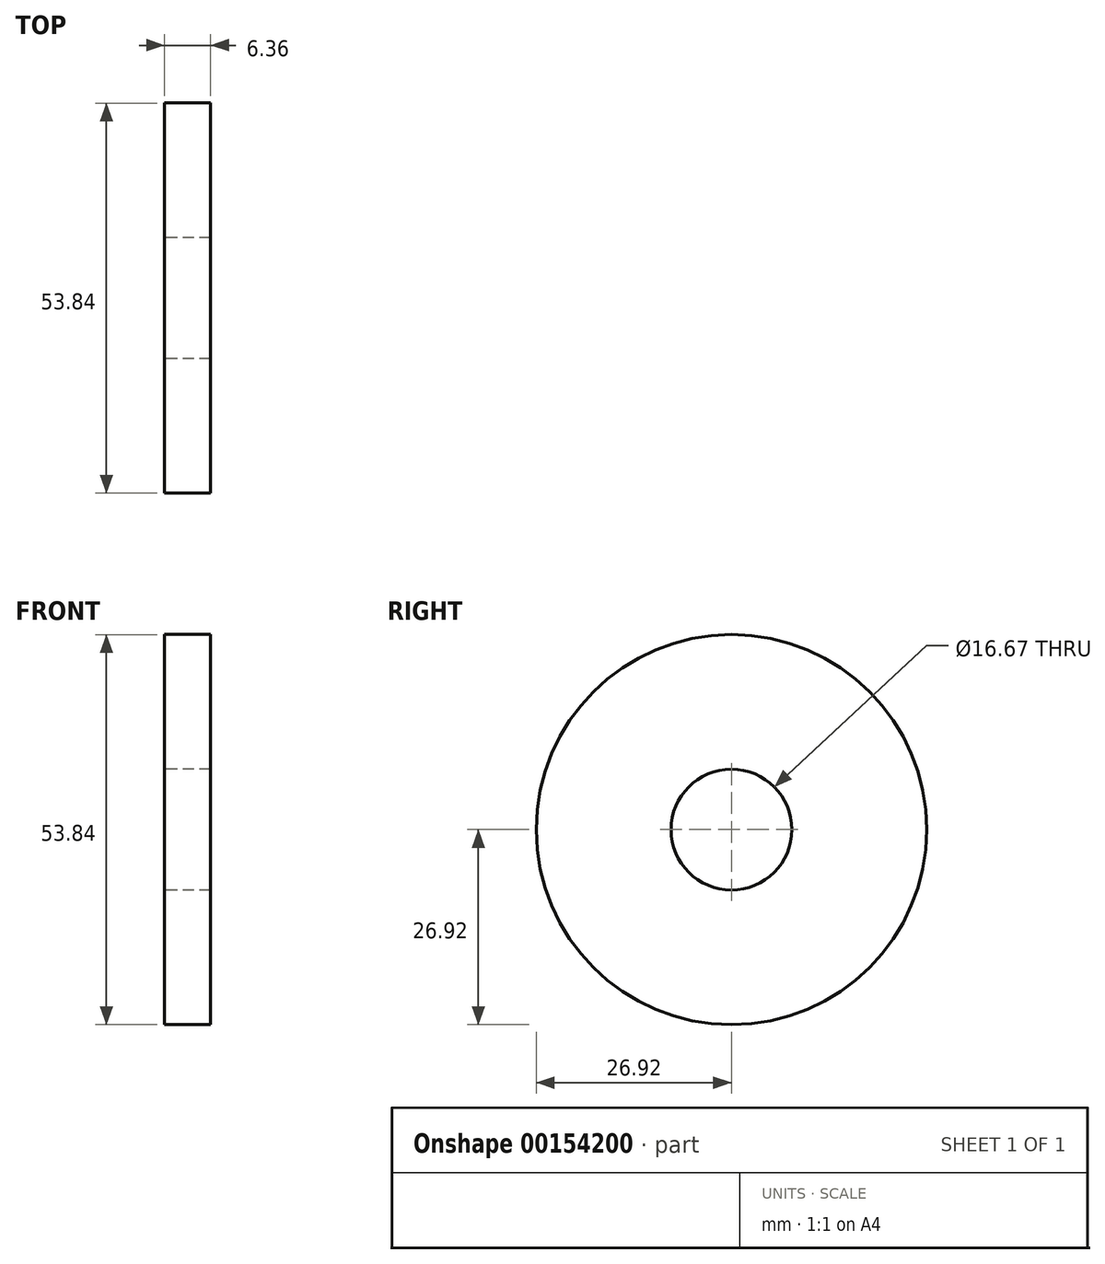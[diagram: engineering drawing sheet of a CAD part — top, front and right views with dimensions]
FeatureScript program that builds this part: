
annotation { "Feature Type Name" : "Feature", "Feature Type Description" : "" }
export const myFeature = defineFeature(function(context is Context, id is Id, definition is map)
    precondition{}
    {
        {
            var Q0;
            Q0=qCreatedBy(makeId("Right.planeOp"),FACE);
            var sketch = newSketch(context, id + "F0", { "sketchPlane" : qUnion([Q0])});
            skCircle(sketch, "E0", {"center": v(0, 0) * mm, "radius": 26.92 * mm});
            skCircle(sketch, "E1", {"center": v(0, 0) * mm, "radius": 8.33 * mm});
            skSolve(sketch);
        }
        {
            var Q0;
            Q0=qSketchRegion(id+"F0",true);
            extrude(context, id + "F1", {"entities" : qUnion([Q0]), "endBound" : BoundingType.SYMMETRIC, "depth" : 6.35 * mm});
        }
    });
